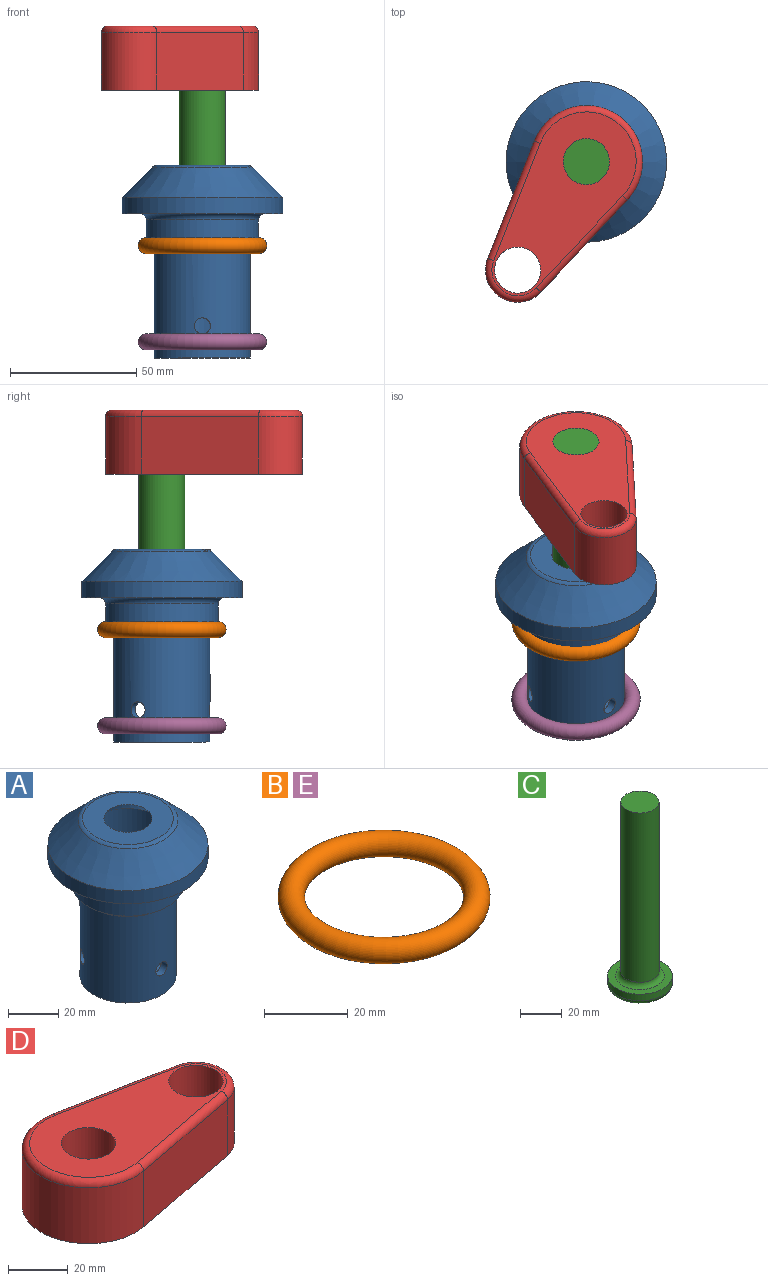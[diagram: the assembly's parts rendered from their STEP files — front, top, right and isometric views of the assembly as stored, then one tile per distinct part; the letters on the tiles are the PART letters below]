
ASSEMBLY  parts=5 mates=4
PART A: 18 faces, bbox 63.5x63.5x76.2 mm
  f0: cylinder r=19.05mm len=41.91mm, axis (0,0,-1), area 4921.4mm2, adj f3,f11,f12,f13,f14
  f1: cylinder r=15.88mm len=60.96mm, axis (0,0,-1), area 5985.3mm2, adj f10,f11,f12,f13,f17
  f2: plane 26.67x26.67mm, normal (0,0,1), area 558.6mm2, adj f17
  f3: plane 38.1x38.1mm, normal (0,0,-1), area 1140.1mm2, adj f0
  f4: plane 44.45x44.45mm, normal (0,0,-1), area 87.4mm2, adj f5,f14
  f5: cylinder r=22.23mm len=44.45mm, axis (0,0,-1), area 1418.8mm2, adj f4,f15
  f6: plane 63.5x63.5mm, normal (0,0,-1), area 1240.2mm2, adj f7,f15
  f7: cylinder r=31.75mm len=63.5mm, axis (0,0,-1), area 1266.8mm2, adj f6,f8
  f8: cone r=31.75mm half-angle=45deg, axis (0,0,-1), area 2738mm2, adj f7,f16
  f9: plane 36x36mm, normal (0,0,1), area 732.6mm2, adj f10,f16
  f10: cone r=15.88mm half-angle=45deg, axis (0,0,-1), area 716.6mm2, adj f1,f9
  f11: cylinder r=3.17mm len=6.35mm, axis (0,1,0), area 63.9mm2, adj f0,f1
  f12: cylinder r=3.17mm len=7.25mm, axis (0.87,-0.5,0), area 63.9mm2, adj f0,f1
  f13: cylinder r=3.17mm len=7.25mm, axis (-0.87,-0.5,0), area 63.9mm2, adj f0,f1
  f14: torus R=21.59mm, axis (0,0,-1), area 500.7mm2, adj f0,f4
  f15: torus R=24.77mm, axis (0,0,-1), area 580.3mm2, adj f5,f6
  f16: torus R=18mm, axis (0,0,1), area 237.5mm2, adj f8,f9
  f17: torus R=13.33mm, axis (0,0,-1), area 374.8mm2, adj f1,f2
PART B: 1 faces, bbox 55x55x6.4 mm
  f0: torus R=22.23mm, axis (0,0,1), area 2785.8mm2
PART C: 7 faces, bbox 33.5x33.5x108 mm
  f0: plane 25.88x25.88mm, normal (0,0,-1), area 525.9mm2, adj f5
  f1: cylinder r=15.48mm len=30.96mm, axis (0,0,-1), area 370.5mm2, adj f2,f5
  f2: plane 30.96x30.96mm, normal (0,0,1), area 324.9mm2, adj f1,f6
  f3: cylinder r=9.13mm len=99.06mm, axis (0,0,-1), area 5681.5mm2, adj f4,f6
  f4: plane 18.26x18.26mm, normal (0,0,1), area 261.8mm2, adj f3
  f5: torus R=12.94mm, axis (0,0,-1), area 364.9mm2, adj f0,f1
  f6: torus R=11.67mm, axis (0,0,-1), area 252mm2, adj f2,f3
PART D: 12 faces, bbox 88.6x48.1x25.4 mm
  f0: cylinder r=22.23mm len=44.45mm, axis (0,0,1), area 1787.8mm2, adj f1,f3,f6,f9
  f1: plane 49.01x22.86mm, normal (0.19,-0.98,0), area 1140.7mm2, adj f0,f2,f6,f11
  f2: cylinder r=12.7mm len=24.95mm, axis (0,0,1), area 802.6mm2, adj f1,f3,f6,f10
  f3: plane 49.01x22.86mm, normal (0.19,0.98,0), area 1140.7mm2, adj f0,f2,f6,f8
  f4: cylinder r=9.13mm len=25.4mm, axis (0,0,1), area 1456.8mm2, adj f6,f7
  f5: cylinder r=9.13mm len=25.4mm, axis (0,0,1), area 1456.8mm2, adj f6,f7
  f6: plane 85.73x44.45mm, normal (0,0,-1), area 2311.2mm2, adj f0,f1,f2,f3,f4,f5
  f7: plane 80.65x39.37mm, normal (0,0,1), area 1790.2mm2, adj f4,f5,f8,f9,f10,f11
  f8: cylinder r=2.54mm len=49.49mm, axis (-0.98,0.19,0), area 199.1mm2, adj f3,f7,f9,f10
  f9: torus R=19.69mm, axis (0,0,1), area 299.1mm2, adj f0,f7,f8,f11
  f10: torus R=10.16mm, axis (0,0,1), area 129.9mm2, adj f2,f7,f8,f11
  f11: cylinder r=2.54mm len=49.49mm, axis (0.98,0.19,0), area 199.1mm2, adj f1,f7,f9,f10
PART E: same geometry as B
PLACE A at identity fixed
PLACE B t=(0,0,44.45)mm
PLACE C rot(axis=(0,0,-1),122.4deg) t=(0,0,17.02)mm
PLACE D rot(axis=(0,0,-1),122.4deg) t=(0,0,17.02)mm
PLACE E t=(0,0,6.35)mm
MATE fastened B.f0 <-> A.f0  axis (0,0,1) through (0,0,44.45)mm
MATE fastened D.f4 <-> C.f1  axis (0,0,1) through (0,0,131.32)mm
MATE fastened A.f0 <-> E.f0  axis (0,0,-1) through (0,0,0)mm
MATE cylindrical A.f0 <-> C.f1  axis (0,0,1) through (0,0,6.35)mm
